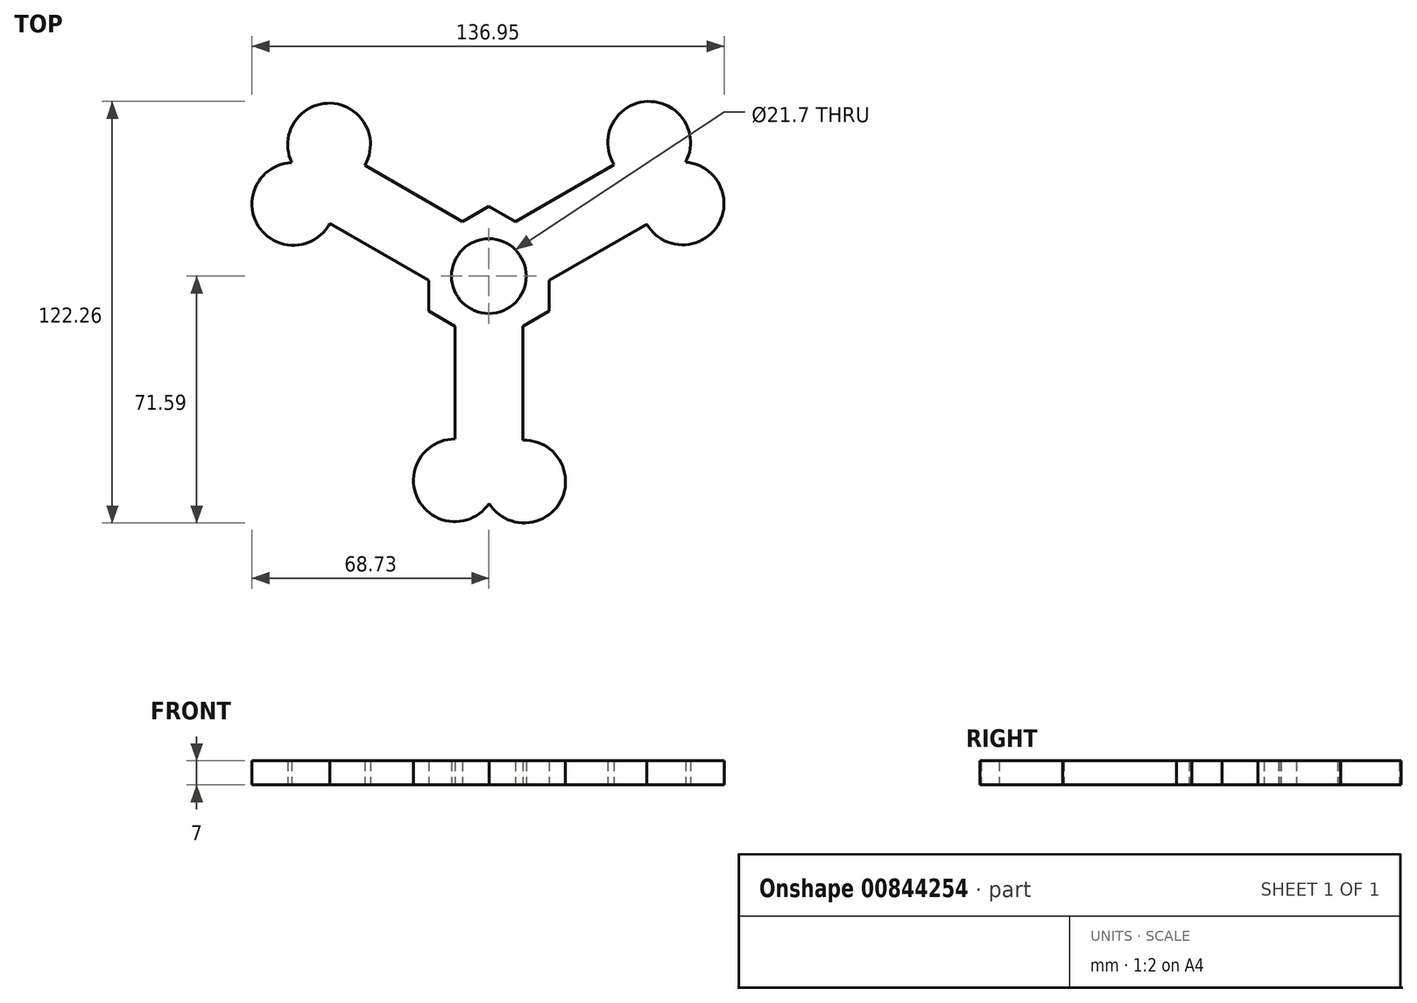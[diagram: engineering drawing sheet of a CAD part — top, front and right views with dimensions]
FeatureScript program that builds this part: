
annotation { "Feature Type Name" : "Feature", "Feature Type Description" : "" }
export const myFeature = defineFeature(function(context is Context, id is Id, definition is map)
    precondition{}
    {
        {
            var Q0;
            Q0=qCreatedBy(makeId("Top.planeOp"),FACE);
            var sketch = newSketch(context, id + "F0", { "sketchPlane" : qUnion([Q0])});
            skLineSegment(sketch, "E0", {"start": v(-9.86, -14.46) * mm, "end": v(-9.86, -47.6) * mm});
            skLineSegment(sketch, "E1", {"start": v(9.86, -14.46) * mm, "end": v(9.86, -47.6) * mm});
            skArc(sketch, "E2", {"start": v(-9.86, -47.22) * mm, "mid": v(-20.46, -64.84) * mm, "end": v(0.07, -65.95) * mm});
            skArc(sketch, "E3", {"start": v(0.07, -65.95) * mm, "mid": v(20.83, -65.24) * mm, "end": v(9.86, -47.6) * mm});
            skLineSegment(sketch, "E4.1.0", {"start": v(17.45, -1.31) * mm, "end": v(46.15, 15.26) * mm});
            skLineSegment(sketch, "E4.1.1", {"start": v(7.59, 15.77) * mm, "end": v(36.29, 32.34) * mm});
            skArc(sketch, "E4.1.2", {"start": v(45.83, 15.07) * mm, "mid": v(66.39, 14.7) * mm, "end": v(57.08, 33.04) * mm});
            skArc(sketch, "E4.1.5", {"start": v(57.08, 33.04) * mm, "mid": v(46.08, 50.66) * mm, "end": v(36.29, 32.34) * mm});
            skLineSegment(sketch, "E4.2.0", {"start": v(-7.59, 15.77) * mm, "end": v(-36.29, 32.34) * mm});
            skLineSegment(sketch, "E4.2.1", {"start": v(-17.45, -1.31) * mm, "end": v(-46.15, 15.26) * mm});
            skArc(sketch, "E4.2.2", {"start": v(-35.96, 32.15) * mm, "mid": v(-45.93, 50.14) * mm, "end": v(-57.15, 32.91) * mm});
            skArc(sketch, "E4.2.5", {"start": v(-57.15, 32.91) * mm, "mid": v(-66.91, 14.58) * mm, "end": v(-46.15, 15.26) * mm});
            skPoint(sketch, "E4.center", {"position": v(0, 0) * mm});
            skArc(sketch, "E5.cCircle", {"start": v(-7.59, 15.77) * mm, "mid": v(-8.17, 15.47) * mm, "end": v(-8.75, 15.16) * mm, "construction": true});
            skLineSegment(sketch, "E5.0", {"start": v(-17.5, -10.1) * mm, "end": v(-17.5, 0) * mm});
            skLineSegment(sketch, "E5.1", {"start": v(-8.75, 15.16) * mm, "end": v(0, 20.2) * mm});
            skLineSegment(sketch, "E5.2", {"start": v(0, 20.2) * mm, "end": v(8.75, 15.16) * mm});
            skLineSegment(sketch, "E5.3", {"start": v(17.5, 0) * mm, "end": v(17.5, -10.1) * mm});
            skLineSegment(sketch, "E5.4", {"start": v(17.5, -10.1) * mm, "end": v(8.75, -15.16) * mm});
            skLineSegment(sketch, "E5.5", {"start": v(-8.75, -15.16) * mm, "end": v(-17.5, -10.1) * mm});
            skPoint(sketch, "E5.0.midPoint", {"position": v(-17.5, 0) * mm});
            skArc(sketch, "E6.trimOffspring", {"start": v(-17.5, 0) * mm, "mid": v(-17.49, -0.66) * mm, "end": v(-17.45, -1.31) * mm, "construction": true});
            skArc(sketch, "E7.trimOffspring", {"start": v(-9.86, -14.46) * mm, "mid": v(-9.31, -14.82) * mm, "end": v(-8.75, -15.16) * mm, "construction": true});
            skArc(sketch, "E8.trimOffspring", {"start": v(8.75, -15.16) * mm, "mid": v(9.31, -14.82) * mm, "end": v(9.86, -14.46) * mm, "construction": true});
            skArc(sketch, "E9.trimOffspring", {"start": v(17.45, -1.31) * mm, "mid": v(17.49, -0.66) * mm, "end": v(17.5, 0) * mm, "construction": true});
            skArc(sketch, "E10.trimOffspring", {"start": v(8.75, 15.16) * mm, "mid": v(8.17, 15.47) * mm, "end": v(7.59, 15.77) * mm, "construction": true});
            skCircle(sketch, "E11", {"center": v(0, 0) * mm, "radius": 10.85 * mm});
            skPoint(sketch, "E12.center.orphan", {"position": v(0, -54.8) * mm});
            skPoint(sketch, "E13.orphan", {"position": v(-9.86, -7.6) * mm});
            skPoint(sketch, "E14.orphan", {"position": v(17.5, 10.1) * mm});
            skPoint(sketch, "E15.orphan", {"position": v(-17.5, 10.1) * mm});
            skPoint(sketch, "E16.orphan", {"position": v(0, -20.2) * mm});
            skSolve(sketch);
        }
        {
            var Q0;
            {var subQ16=sQuery(id+"F0.wireOp",EDGE,"E2");Q0=makeQuery(id+"F0.imprint","IMPRINT",FACE,{"disambiguationData":[TD([[makeQuery(id+"F0.imprint","IMPRINT",EDGE,{"derivedFrom":subQ16}),1.0]])]});}
            extrude(context, id + "F1", {"entities" : qUnion([Q0]), "depth" : 7 * mm, "offsetDistance" : 25 * mm});
        }
    });
